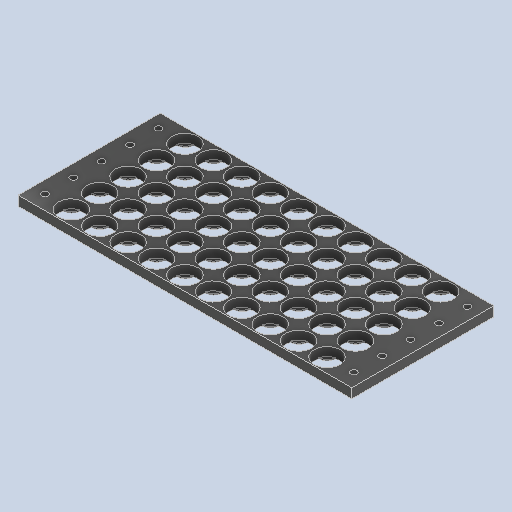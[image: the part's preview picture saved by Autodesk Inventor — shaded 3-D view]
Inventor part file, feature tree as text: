
AUTODESK INVENTOR PART (.ipt)
format: ipt  version: 2023 (Build 270158000, 158)  size: 12,485,120 bytes
history: native  units: in
note: dims shown in document units (in); Inventor stores cm internally (conversion verified against a paired STEP export)
features: extrude x3, sketch x2, pattern_linear x1
ambient origin geometry x8: Origin, YZ Plane, XZ Plane, XY Plane, X Axis, Y Axis, Z Axis, Center Point
bodies: Solid1 (feature_tree)
feature tree (6):
  sketch  "Sketch1"  dims[d0=0.8268in d1=0.9055in]
  extrude  "Extrusion1"  Depth=0.9055in
  extrude  "Extrusion2"  Depth=0.3937in TaperAngle=360.0deg
  pattern_linear  "Rectangular Pattern1"  Spacing1=0.0315in  [1 undecoded]
  extrude  "Extrusion3"  Depth=0.9055in
  sketch  "Sketch2"  dims[d2=0.2756in d3=0.0in d4=1.5748in d6=360.0deg d8=0.0315in d9=0.0in d10=3.937in d12=0.9055in d13=1.9685in d15=0.9055in d16=0.7874in d17=0.2047in d18=0.3937in d19=0.0in d20=0.0197in d21=0.0344in d22=0.0197in d23=0.0344in]
note: 1 required parameter value undecoded (feature->parameter linkage not recoverable at this tier; creation-order binding heuristic only, values carry confidence <= 0.55)
